# Revit family: SCVW
name_source: partatom
category: Lighting Fixtures
units: mm (PartAtom-declared; Revit-internal decimal feet)

## family parameters
Cut with Voids When Loaded = No
Host = Face
Light Source = Yes
OmniClass Number = 23.80.70.11
OmniClass Title = Luminaries for Internal Lighting
Part Type = Normal
Room Calculation Point = No
Round Connector Dimension = Use Diameter
Shared = Yes

## types (1)
- SCVW
    Apparent Load = 0 VA
    Applications = Extreme Environment
Food Processing
Cold Storage
Wash Down
Food Preparation
Agricultural Buildings
Wet Location
Transporation
Stairwells
Corridors
Entry Ways
Awnings
Warehouses
    Backbox = White
    Certifications = CSA
cUL
UL Sanitation certified per NSF standards
    Color Filter = 16777215
    Default Elevation = 4.0'
    Description = SCVW is a multi-functional enclosed Antimicrobial Lighting LED product which serves rugged to severe conditions as well as food service areas. SCVW can be ordered in dependent or independent SpectraClean™ modes.
    Dimming Lamp Color Temperature Shift = <None>
    Emit from Line Length = 2.0'
    Features = Option 1: Independent — Alternates between pure white light and Dediciated SpectraClean mode for scheduled maximum disinfection
Option 2: Dedicated — Concentrated SpectraClean (405 nm only) mode formaximum disinfection
Impact resistant frosted acrylic lens or optional frosted polycarbonate lens
Removable gear tray electrical access
-40°C (-104°F) up to +30°C (86°F) ambient operation; see table providedfor details
    Glass = White Glass
    IP Rating = IP67
    Lamp = LED Lamp
    Manufacturer = Columbia Lighting
    Model = SCVW
    Nominal Watts = 102 W
    Photometric Web File = generic.ies
    Row Length = 4.0'
    Tilt Angle = -90.00°
    URL = " Columbia Lighting"
    Voltage = 120 V
    Warranty = 5 Year Limited Warranty

## geometry (parser evidence)
native form markers: Blend x1, Sweep x6
no freeform markers — native parametric forms only
